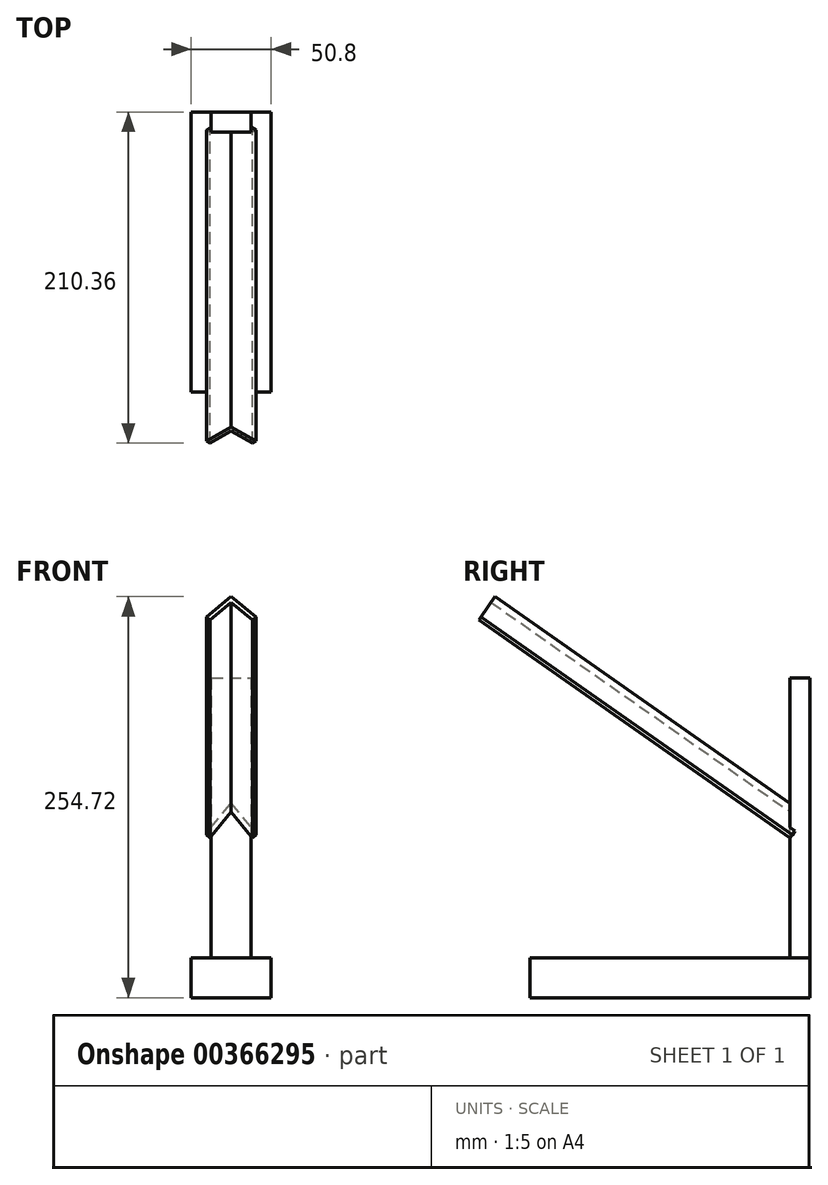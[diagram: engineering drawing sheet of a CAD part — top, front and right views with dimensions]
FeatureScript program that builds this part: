
annotation { "Feature Type Name" : "Feature", "Feature Type Description" : "" }
export const myFeature = defineFeature(function(context is Context, id is Id, definition is map)
    precondition{}
    {
        {
            var Q0;
            Q0=qCreatedBy(makeId("Top.planeOp"),FACE);
            var sketch = newSketch(context, id + "F0", { "sketchPlane" : qUnion([Q0])});
            skLineSegment(sketch, "E0.bottom", {"start": v(-25.4, 12.7) * mm, "end": v(25.4, 12.7) * mm});
            skLineSegment(sketch, "E0.top", {"start": v(-25.4, -165.1) * mm, "end": v(25.4, -165.1) * mm});
            skLineSegment(sketch, "E0.left", {"start": v(-25.4, 12.7) * mm, "end": v(-25.4, -165.1) * mm});
            skLineSegment(sketch, "E0.right", {"start": v(25.4, 12.7) * mm, "end": v(25.4, -165.1) * mm});
            skSolve(sketch);
        }
        {
            var Q0;
            Q0 = qSketchRegion(id + "F0", true);
            extrude(context, id + "F1", {"entities" : qUnion([Q0]), "oppositeDirection" : true, "depth" : 25.4 * mm});
        }
        {
            var Q0;
            Q0=qCreatedBy(makeId("Top.planeOp"),FACE);
            cPlane(context, id + "F2", {"entities" : qUnion([Q0]), "cplaneType" : CPlaneType.OFFSET, "offset" : 76.2 * mm, "width" : 152.4 * mm, "height" : 152.4 * mm});
        }
        {
            var Q0;
            Q0=qCreatedBy(id+"F2.planeOp",FACE);
            var sketch = newSketch(context, id + "F3", { "sketchPlane" : qUnion([Q0])});
            skLineSegment(sketch, "E1.bottom", {"start": v(-12.7, 0) * mm, "end": v(12.7, 0) * mm});
            skLineSegment(sketch, "E1.top", {"start": v(-12.7, 12.7) * mm, "end": v(12.7, 12.7) * mm});
            skLineSegment(sketch, "E1.left", {"start": v(-12.7, 0) * mm, "end": v(-12.7, 12.7) * mm});
            skLineSegment(sketch, "E1.right", {"start": v(12.7, 0) * mm, "end": v(12.7, 12.7) * mm});
            skSolve(sketch);
        }
        {
            var Q0;
            Q0 = qSketchRegion(id + "F3", true);
            extrude(context, id + "F4", {"entities" : qUnion([Q0]), "operationType" : NewBodyOperationType.ADD, "endBound" : BoundingType.SYMMETRIC, "depth" : 203.2 * mm});
        }
        {
            var Q0;
            Q0=qCreatedBy(id+"F2.planeOp",FACE);
            var sketch = newSketch(context, id + "F5", { "sketchPlane" : qUnion([Q0])});
            skLineSegment(sketch, "E2", {"start": v(-14.45, 0) * mm, "end": v(15.68, 0) * mm});
            skSolve(sketch);
        }
        {
            var Q0;
            Q0=sQuery(id+"F5.wireOp",EDGE,"E2");
            cPlane(context, id + "F6", {"entities" : qUnion([Q0]), "cplaneType" : CPlaneType.LINE_ANGLE, "offset" : 25.4 * mm, "angle" : 35 * degree, "oppositeDirection" : true, "width" : 152.4 * mm, "height" : 152.4 * mm});
        }
        {
            var Q0;
            Q0=qCreatedBy(id+"F6.planeOp",FACE);
            var sketch = newSketch(context, id + "F7", { "sketchPlane" : qUnion([Q0])});
            skLineSegment(sketch, "E3", {"start": v(0, 75.89) * mm, "end": v(13.47, 62.42) * mm});
            skLineSegment(sketch, "E4", {"start": v(13.47, 62.42) * mm, "end": v(15.72, 64.66) * mm});
            skLineSegment(sketch, "E5", {"start": v(15.72, 64.66) * mm, "end": v(0, 80.38) * mm});
            skLineSegment(sketch, "E6", {"start": v(0, 80.38) * mm, "end": v(-15.72, 64.66) * mm});
            skLineSegment(sketch, "E7", {"start": v(-15.72, 64.66) * mm, "end": v(-13.47, 62.42) * mm});
            skLineSegment(sketch, "E8", {"start": v(-13.47, 62.42) * mm, "end": v(0, 75.89) * mm});
            skSolve(sketch);
        }
        {
            var Q0;
            Q0 = qSketchRegion(id + "F7", true);
            extrude(context, id + "F8", {"entities" : qUnion([Q0]), "operationType" : NewBodyOperationType.ADD, "oppositeDirection" : true, "depth" : 241.3 * mm});
        }
    });
